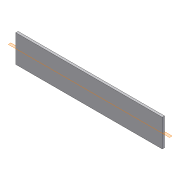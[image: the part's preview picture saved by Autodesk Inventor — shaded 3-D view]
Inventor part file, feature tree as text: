
AUTODESK INVENTOR PART (.ipt)
format: ipt  version: 2012 (Build 160160000, 160)  size: 62,976 bytes
history: native  units: in
note: dims shown in document units (in); Inventor stores cm internally (conversion verified against a paired STEP export)
features: extrude x1, plane x1, sketch x1
ambient origin geometry x8: Origin, YZ Plane, XZ Plane, XY Plane, X Axis, Y Axis, Z Axis, Center Point
bodies: Solid1 (feature_tree)
feature tree (3):
  extrude  "Extrusion1"  Depth=3.0in
  plane  "Work Plane2"
  sketch  "Sketch1"  dims[d0=16.0in d1=3.0in d2=0.25in d3=0.0in d5=-1.5in]
